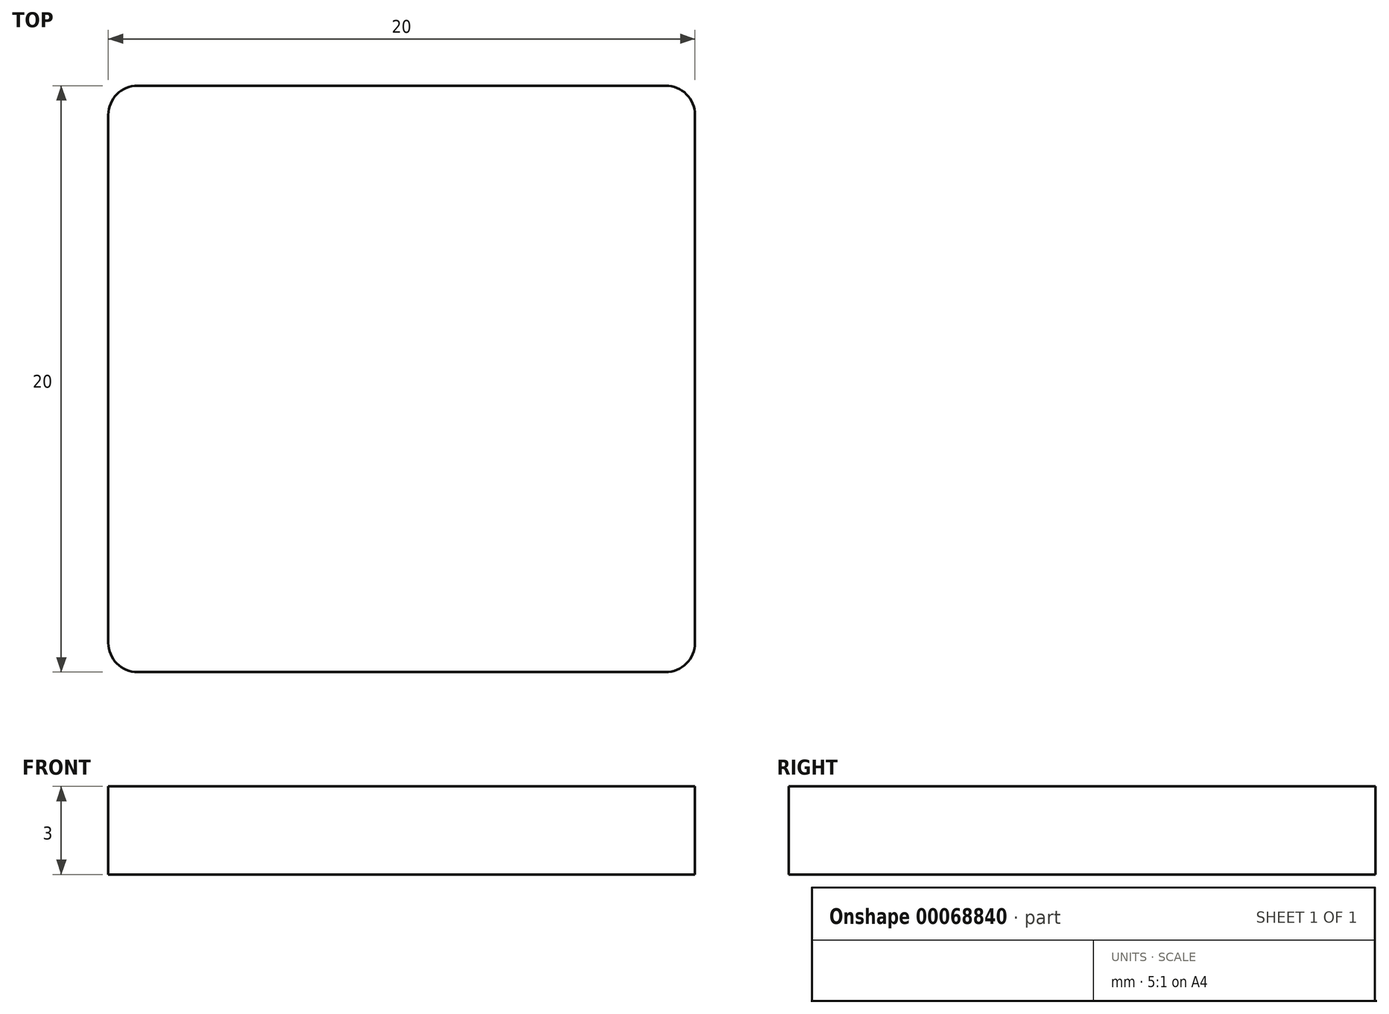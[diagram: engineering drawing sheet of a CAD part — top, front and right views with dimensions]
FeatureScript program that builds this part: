
annotation { "Feature Type Name" : "Feature", "Feature Type Description" : "" }
export const myFeature = defineFeature(function(context is Context, id is Id, definition is map)
    precondition{}
    {
        {
            var Q0;
            Q0=qCreatedBy(makeId("Top.planeOp"),FACE);
            var sketch = newSketch(context, id + "F0", { "sketchPlane" : qUnion([Q0])});
            skLineSegment(sketch, "E0.rect.bottom", {"start": v(9, 10) * mm, "end": v(-9, 10) * mm});
            skLineSegment(sketch, "E0.rect.top", {"start": v(9, -10) * mm, "end": v(-9, -10) * mm});
            skLineSegment(sketch, "E0.rect.left", {"start": v(10, 9) * mm, "end": v(10, -9) * mm});
            skLineSegment(sketch, "E0.rect.right", {"start": v(-10, 9) * mm, "end": v(-10, -9) * mm});
            skPoint(sketch, "E0.rect.middle", {"position": v(0, 0) * mm});
            skPoint(sketch, "E1.visualSharp", {"position": v(-10, 10) * mm});
            skArc(sketch, "E1.filletArc", {"start": v(-9, 10) * mm, "mid": v(-9.7, 9.7) * mm, "end": v(-10, 9) * mm});
            skPoint(sketch, "E2.visualSharp", {"position": v(10, 10) * mm});
            skArc(sketch, "E2.filletArc", {"start": v(10, 9) * mm, "mid": v(9.7, 9.7) * mm, "end": v(9, 10) * mm});
            skPoint(sketch, "E3.visualSharp", {"position": v(10, -10) * mm});
            skArc(sketch, "E3.filletArc", {"start": v(9, -10) * mm, "mid": v(9.7, -9.7) * mm, "end": v(10, -9) * mm});
            skPoint(sketch, "E4.visualSharp", {"position": v(-10, -10) * mm});
            skArc(sketch, "E4.filletArc", {"start": v(-10, -9) * mm, "mid": v(-9.7, -9.7) * mm, "end": v(-9, -10) * mm});
            skSolve(sketch);
        }
        {
            var Q0;
            Q0=makeQuery(id+"F0.imprint","IMPRINT",FACE,{"disambiguationData":[TD([[makeQuery(id+"F0.imprint","IMPRINT",EDGE,{"derivedFrom":sQuery(id+"F0.wireOp",EDGE,"E0.rect.bottom")}),1.0]])]});
            extrude(context, id + "F1", {"entities" : qUnion([Q0]), "depth" : 3 * mm});
        }
    });
